# Revit family: P710097-031
name_source: partatom
category: Lighting Fixtures
units: mm (PartAtom-declared; Revit-internal decimal feet)

## family parameters
Cut with Voids When Loaded = No
Host = Face
Light Source = Yes
OmniClass Number = 23.80.70.11.14.17
OmniClass Title = Direct/Indirect
Part Type = Normal
Room Calculation Point = No
Round Connector Dimension = Use Diameter
Shared = Yes

## types (1)
- P710097-031
    Apparent Load = 60 VA
    Assembly Code = D5020200
    Ballast = Paint - Hubbell - Carbon Black
    Color Filter = 16777215
    Connector Description = Lighting Connector
    Default Elevation = 48 "
    Description = Stockbrace Collection One-Light Matte Black and Clear Glass Farmhouse Style Wall Light
    Dimming Lamp Color Temperature Shift = <None>
    Features = Application: Inspired by traditional post-and-beam construction, the Stockbrace Collection 1-Light Matte Black Clear Glass Farmhouse Wall Light ideal for any entryway, hallway, foyer, bedroom, sitting room, living room, or bathroom.
Styles: Perfect for modern farmhouse style settings.
Finish: Clean lines, an open design, and architectural details are coated in a classic matte black finish.
Materials: Constructed from steel to ensure a long product lifespan.
Glass/Shades: A light source illuminates a clear glass shade to complete the clean design.
Bulbs: For ideal illumination, use 1 medium base bulbs that are sold separately (60w max - LED/CFL/incandescent). Compatible with dimmable bulbs.
Dimensions: Measures 4-3/4-inch width by 13-1/2-inch height.
Certifications: cULus damp location listed.
Pairs With: Pairs with the Briarwood, Lockhart, and Clarion collections from Progress Lighting.
Warranty: Our 1-Year Limited Warranty guarantees your complete satisfaction with your purchase and includes professional after-sales customer service support.
    Fixture distribution = Direct
    Glass = Paint - Hubbell - White Texture
    Gold = Hubbell - Gold
    Housing Material = Paint - Hubbell - Carbon Black
    Lamp = LED/CFL/incandescent
    Length = 7.5 "
    Load Classification = Lighting
    Manufacturer = Progress Lighting
    Model = P710097-031
    Photometric Web File = generic.ies
    Power Factor = 1
    Product Documentation Link = https://hubbellcdn.com
    Product Link = https://www.hubbell.com
    Reflector = Glass - Hubbell - Glass
    Tilt Angle = 180.00°
    URL = https://www.hubbell.com
    Voltage = 120 V
    Warranty = 1 year Warranty
    Wattage Comments = 60W
    Watts = 60 W
    Width = 4.75 "

## geometry (parser evidence)
native form markers: Sweep x5
no freeform markers — native parametric forms only
